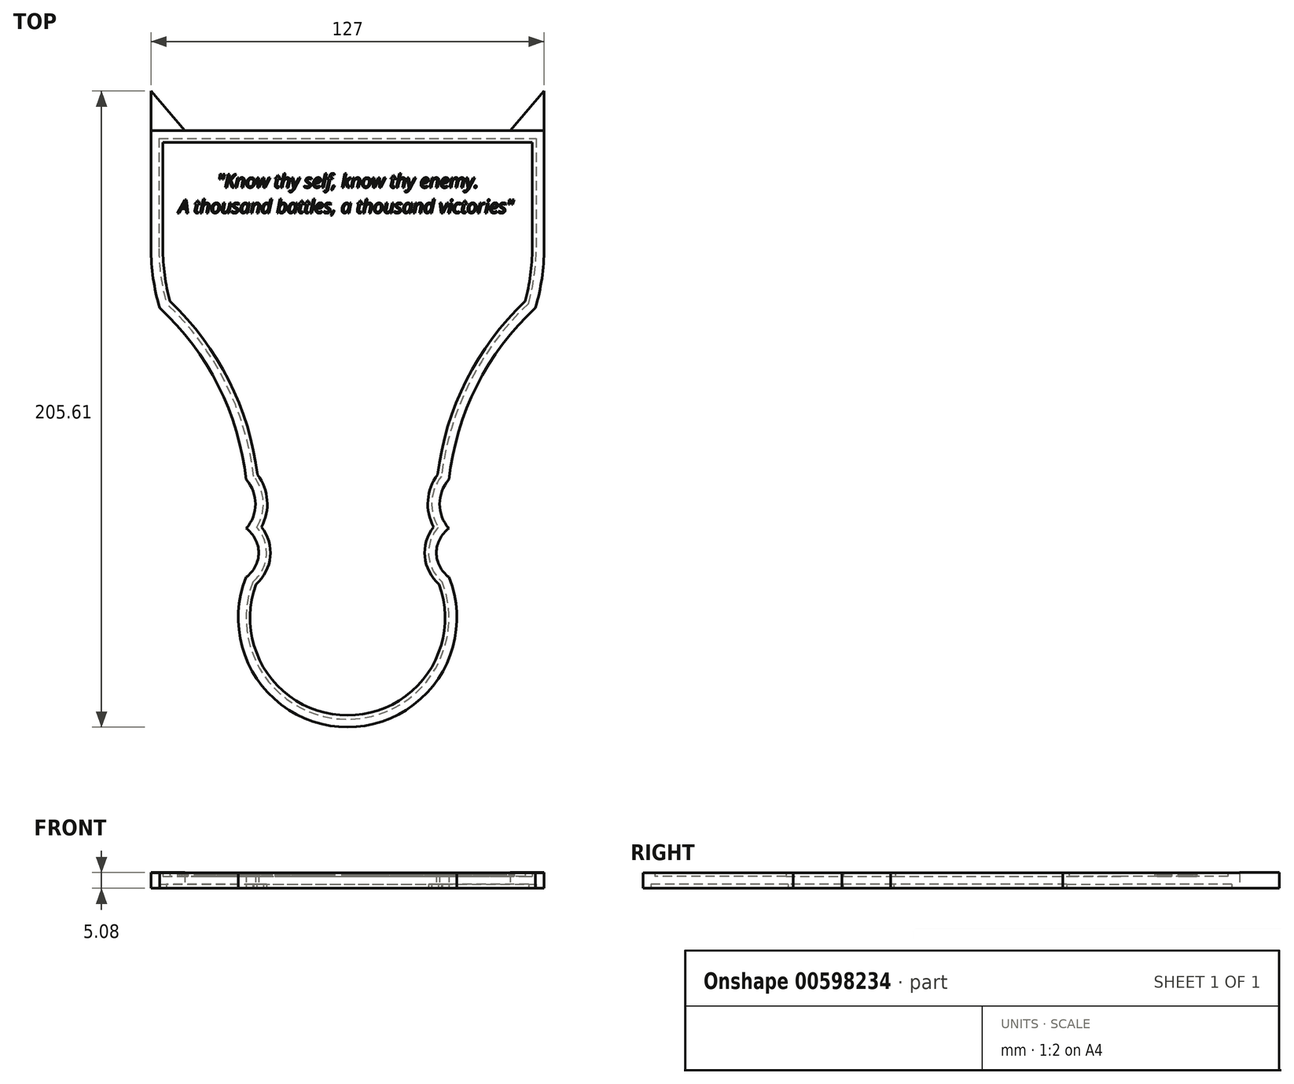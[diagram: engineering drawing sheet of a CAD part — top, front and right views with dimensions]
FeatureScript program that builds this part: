
annotation { "Feature Type Name" : "Feature", "Feature Type Description" : "" }
export const myFeature = defineFeature(function(context is Context, id is Id, definition is map)
    precondition{}
    {
        {
            var Q0;
            Q0=qCreatedBy(makeId("Top.planeOp"),FACE);
            var sketch = newSketch(context, id + "F0", { "sketchPlane" : qUnion([Q0])});
            skLineSegment(sketch, "E0", {"start": v(0, 0) * mm, "end": v(0, 57.26) * mm});
            skLineSegment(sketch, "E1", {"start": v(0, 57.26) * mm, "end": v(-63.5, 57.26) * mm});
            skLineSegment(sketch, "E2", {"start": v(0, 57.26) * mm, "end": v(63.5, 57.26) * mm});
            skLineSegment(sketch, "E3", {"start": v(-63.5, 57.26) * mm, "end": v(-63.5, 19.16) * mm});
            skLineSegment(sketch, "E4", {"start": v(63.5, 57.26) * mm, "end": v(63.5, 19.16) * mm});
            skArc(sketch, "E5", {"start": v(-63.5, 19.16) * mm, "mid": v(-62.8, 9.48) * mm, "end": v(-60.74, 0) * mm});
            skArc(sketch, "E6", {"start": v(-32.75, -55.58) * mm, "mid": v(-41.76, -25.28) * mm, "end": v(-60.74, 0) * mm});
            skArc(sketch, "E7", {"start": v(-32.75, -71.34) * mm, "mid": v(-29.74, -63.46) * mm, "end": v(-32.75, -55.58) * mm});
            skArc(sketch, "E8", {"start": v(-32.75, -87.08) * mm, "mid": v(-28.73, -79.2) * mm, "end": v(-32.75, -71.34) * mm});
            skArc(sketch, "E9.MirrorCS", {"start": v(32.75, -71.34) * mm, "mid": v(29.74, -63.46) * mm, "end": v(32.75, -55.58) * mm});
            skArc(sketch, "E10.MirrorCS", {"start": v(32.75, -87.08) * mm, "mid": v(28.73, -79.2) * mm, "end": v(32.75, -71.34) * mm});
            skArc(sketch, "E11.MirrorCS", {"start": v(63.5, 19.16) * mm, "mid": v(62.8, 9.48) * mm, "end": v(60.74, 0) * mm});
            skArc(sketch, "E12.MirrorCS", {"start": v(32.75, -55.58) * mm, "mid": v(41.76, -25.28) * mm, "end": v(60.74, 0) * mm});
            skPoint(sketch, "E13.second.point", {"position": v(32.75, -122.14) * mm});
            skArc(sketch, "E14", {"start": v(-32.75, -87.08) * mm, "mid": v(0, -135.59) * mm, "end": v(32.75, -87.08) * mm});
            skLineSegment(sketch, "E15", {"start": v(-63.5, 57.26) * mm, "end": v(-63.5, 70.02) * mm});
            skLineSegment(sketch, "E16", {"start": v(-63.5, 70.02) * mm, "end": v(-52.59, 57.26) * mm});
            skLineSegment(sketch, "E17", {"start": v(-52.59, 57.26) * mm, "end": v(-63.5, 57.26) * mm});
            skLineSegment(sketch, "E18.MirrorCS", {"start": v(63.5, 57.26) * mm, "end": v(63.5, 70.02) * mm});
            skLineSegment(sketch, "E19.MirrorCS", {"start": v(63.5, 70.02) * mm, "end": v(52.59, 57.26) * mm});
            skLineSegment(sketch, "E20.MirrorCS", {"start": v(52.59, 57.26) * mm, "end": v(63.5, 57.26) * mm});
            skSolve(sketch);
        }
        {
            var Q0;
            Q0=makeQuery(id+"F0.imprint","IMPRINT",FACE,{"disambiguationData":[TD([[makeQuery(id+"F0.imprint","IMPRINT",EDGE,{"derivedFrom":sQuery(id+"F0.wireOp",EDGE,"E1")}),1.0]])]});
            extrude(context, id + "F1", {"entities" : qUnion([Q0]), "depth" : 5 * mm, "offsetDistance" : 25.4 * mm});
        }
        {
            var Q0;
            Q0=makeQuery(id+"F1.opExtrude","CAP_FACE",FACE,{"disambiguationData":[OSD([sQuery(id+"F0.wireOp",EDGE,"E1"),sQuery(id+"F0.wireOp",EDGE,"E2"),sQuery(id+"F0.wireOp",EDGE,"E3"),sQuery(id+"F0.wireOp",EDGE,"E4"),sQuery(id+"F0.wireOp",EDGE,"E5"),sQuery(id+"F0.wireOp",EDGE,"E6"),sQuery(id+"F0.wireOp",EDGE,"E7"),sQuery(id+"F0.wireOp",EDGE,"E8"),sQuery(id+"F0.wireOp",EDGE,"E9.MirrorCS"),sQuery(id+"F0.wireOp",EDGE,"E10.MirrorCS"),sQuery(id+"F0.wireOp",EDGE,"E11.MirrorCS"),sQuery(id+"F0.wireOp",EDGE,"E12.MirrorCS"),sQuery(id+"F0.wireOp",EDGE,"E14")])],"isStart":false});
            shell(context, id + "F2", {"entities" : qUnion([Q0]), "thickness" : 3.8 * mm});
        }
        {
            var Q0;
            Q0=makeQuery(id+"F1.opExtrude","CAP_FACE",FACE,{"disambiguationData":[OSD([sQuery(id+"F0.wireOp",EDGE,"E1"),sQuery(id+"F0.wireOp",EDGE,"E2"),sQuery(id+"F0.wireOp",EDGE,"E3"),sQuery(id+"F0.wireOp",EDGE,"E4"),sQuery(id+"F0.wireOp",EDGE,"E5"),sQuery(id+"F0.wireOp",EDGE,"E6"),sQuery(id+"F0.wireOp",EDGE,"E7"),sQuery(id+"F0.wireOp",EDGE,"E8"),sQuery(id+"F0.wireOp",EDGE,"E9.MirrorCS"),sQuery(id+"F0.wireOp",EDGE,"E10.MirrorCS"),sQuery(id+"F0.wireOp",EDGE,"E11.MirrorCS"),sQuery(id+"F0.wireOp",EDGE,"E12.MirrorCS"),sQuery(id+"F0.wireOp",EDGE,"E14")])],"isStart":true});
            shell(context, id + "F3", {"entities" : qUnion([Q0]), "thickness" : 2.54 * mm});
        }
        {
            var Q0;
            Q0=makeQuery(id+"F1.opExtrude","SWEPT_FACE",FACE,{"disambiguationData":[OSD([sQuery(id+"F0.wireOp",EDGE,"E1"),sQuery(id+"F0.wireOp",EDGE,"E2")])]});
            var sketch = newSketch(context, id + "F4", { "sketchPlane" : qUnion([Q0])});
            skLineSegment(sketch, "E21", {"start": v(0, 0) * mm, "end": v(0, 5) * mm});
            skLineSegment(sketch, "E22", {"start": v(0, 5) * mm, "end": v(0, 2.5) * mm});
            skLineSegment(sketch, "E23", {"start": v(0, 2.5) * mm, "end": v(63.5, 2.5) * mm});
            skLineSegment(sketch, "E24", {"start": v(63.5, 2.5) * mm, "end": v(0, 2.5) * mm});
            skLineSegment(sketch, "E25", {"start": v(-63.5, 2.5) * mm, "end": v(0, 2.5) * mm});
            skCircle(sketch, "E26", {"center": v(-3.5, 2.5) * mm, "radius": 2.54 * mm});
            skCircle(sketch, "E27", {"center": v(-10.52, 2.5) * mm, "radius": 2.54 * mm});
            skCircle(sketch, "E28", {"center": v(-17.53, 2.5) * mm, "radius": 2.54 * mm});
            skCircle(sketch, "E29", {"center": v(-24.54, 2.5) * mm, "radius": 2.54 * mm});
            skCircle(sketch, "E30", {"center": v(-31.55, 2.5) * mm, "radius": 2.54 * mm});
            skCircle(sketch, "E31", {"center": v(-38.56, 2.5) * mm, "radius": 2.54 * mm});
            skCircle(sketch, "E32", {"center": v(-45.57, 2.5) * mm, "radius": 2.54 * mm});
            skCircle(sketch, "E33", {"center": v(-52.58, 2.5) * mm, "radius": 2.54 * mm});
            skCircle(sketch, "E34", {"center": v(-59.59, 2.5) * mm, "radius": 2.54 * mm});
            skCircle(sketch, "E35.MirrorC", {"center": v(3.5, 2.5) * mm, "radius": 2.54 * mm});
            skCircle(sketch, "E36.MirrorC", {"center": v(10.52, 2.5) * mm, "radius": 2.54 * mm});
            skCircle(sketch, "E37.MirrorC", {"center": v(17.53, 2.5) * mm, "radius": 2.54 * mm});
            skCircle(sketch, "E38.MirrorC", {"center": v(24.54, 2.5) * mm, "radius": 2.54 * mm});
            skCircle(sketch, "E39.MirrorC", {"center": v(31.55, 2.5) * mm, "radius": 2.54 * mm});
            skCircle(sketch, "E40.MirrorC", {"center": v(38.56, 2.5) * mm, "radius": 2.54 * mm});
            skCircle(sketch, "E41.MirrorC", {"center": v(45.57, 2.5) * mm, "radius": 2.54 * mm});
            skCircle(sketch, "E42.MirrorC", {"center": v(52.58, 2.5) * mm, "radius": 2.54 * mm});
            skCircle(sketch, "E43.MirrorC", {"center": v(59.59, 2.5) * mm, "radius": 2.54 * mm});
            skSolve(sketch);
        }
        {
            var Q0;
            Q0=sQuery(id+"F4.wireOp",EDGE,"E34");
            var Q1;
            Q1=sQuery(id+"F4.wireOp",EDGE,"E33");
            var Q2;
            Q2=sQuery(id+"F4.wireOp",EDGE,"E32");
            var Q3;
            Q3=sQuery(id+"F4.wireOp",EDGE,"E31");
            var Q4;
            Q4=sQuery(id+"F4.wireOp",EDGE,"E30");
            var Q5;
            Q5=sQuery(id+"F4.wireOp",EDGE,"E29");
            var Q6;
            Q6=sQuery(id+"F4.wireOp",EDGE,"E28");
            var Q7;
            Q7=sQuery(id+"F4.wireOp",EDGE,"E27");
            var Q8;
            Q8=sQuery(id+"F4.wireOp",EDGE,"E26");
            var Q9;
            Q9=sQuery(id+"F4.wireOp",EDGE,"E35.MirrorC");
            var Q10;
            Q10=sQuery(id+"F4.wireOp",EDGE,"E36.MirrorC");
            var Q11;
            Q11=sQuery(id+"F4.wireOp",EDGE,"E37.MirrorC");
            var Q12;
            Q12=sQuery(id+"F4.wireOp",EDGE,"E38.MirrorC");
            var Q13;
            Q13=sQuery(id+"F4.wireOp",EDGE,"E39.MirrorC");
            var Q14;
            Q14=sQuery(id+"F4.wireOp",EDGE,"E40.MirrorC");
            var Q15;
            Q15=sQuery(id+"F4.wireOp",EDGE,"E41.MirrorC");
            var Q16;
            Q16=sQuery(id+"F4.wireOp",EDGE,"E42.MirrorC");
            var Q17;
            Q17=sQuery(id+"F4.wireOp",EDGE,"E43.MirrorC");
            extrude(context, id + "F5", {"bodyType" : ToolBodyType.SURFACE, "surfaceEntities" : qUnion([Q0, Q1, Q2, Q3, Q4, Q5, Q6, Q7, Q8, Q9, Q10, Q11, Q12, Q13, Q14, Q15, Q16, Q17]), "depth" : 165.1 * mm, "offsetDistance" : 25.4 * mm});
        }
        {
            var Q0;
            Q0=makeQuery(id+"F0.imprint","IMPRINT",FACE,{"disambiguationData":[TD([[makeQuery(id+"F0.imprint","IMPRINT",EDGE,{"derivedFrom":sQuery(id+"F0.wireOp",EDGE,"E18.MirrorCS")}),1.0]])]});
            extrude(context, id + "F6", {"entities" : qUnion([Q0]), "operationType" : NewBodyOperationType.ADD, "depth" : 5.08 * mm, "offsetDistance" : 25.4 * mm});
        }
        {
            var Q0;
            Q0=makeQuery(id+"F0.imprint","IMPRINT",FACE,{"disambiguationData":[TD([[makeQuery(id+"F0.imprint","IMPRINT",EDGE,{"derivedFrom":sQuery(id+"F0.wireOp",EDGE,"E15")}),-1.0]])]});
            extrude(context, id + "F7", {"entities" : qUnion([Q0]), "operationType" : NewBodyOperationType.ADD, "depth" : 5.08 * mm, "offsetDistance" : 25.4 * mm});
        }
        {
            var Q0;
            Q0=makeQuery(id+"F2.opShell","OFFSET_FACE",FACE,{"disambiguationData":[OSD([sQuery(id+"F0.wireOp",EDGE,"E1"),sQuery(id+"F0.wireOp",EDGE,"E2"),sQuery(id+"F0.wireOp",EDGE,"E3"),sQuery(id+"F0.wireOp",EDGE,"E4"),sQuery(id+"F0.wireOp",EDGE,"E5"),sQuery(id+"F0.wireOp",EDGE,"E6"),sQuery(id+"F0.wireOp",EDGE,"E7"),sQuery(id+"F0.wireOp",EDGE,"E8"),sQuery(id+"F0.wireOp",EDGE,"E9.MirrorCS"),sQuery(id+"F0.wireOp",EDGE,"E10.MirrorCS"),sQuery(id+"F0.wireOp",EDGE,"E11.MirrorCS"),sQuery(id+"F0.wireOp",EDGE,"E12.MirrorCS"),sQuery(id+"F0.wireOp",EDGE,"E14"),sQuery(id+"F0.wireOp",EDGE,"E17"),sQuery(id+"F0.wireOp",EDGE,"E20.MirrorCS")])]});
            var sketch = newSketch(context, id + "F8", { "sketchPlane" : qUnion([Q0])});
            skLineSegment(sketch, "E44", {"start": v(0, 0) * mm, "end": v(0, 53.45) * mm});
            skText(sketch, "E45", { "text": "        \"Know thy self, know thy enemy. \nA thousand battles, a thousand victories\"\n", "fontName": "OpenSans-Italic.ttf"});
            const initialGuessF8  = {"E45": [-0.05461, 0.03879, 1, 0, 0.00433]};
            skSetInitialGuess(sketch, initialGuessF8);
            skSolve(sketch);
        }
        {
            var Q0;
            Q0 = qSketchRegion(id + "F8", true);
            extrude(context, id + "F9", {"entities" : qUnion([Q0]), "operationType" : NewBodyOperationType.ADD, "depth" : 0.86 * mm, "offsetDistance" : 25.4 * mm});
        }
    });
